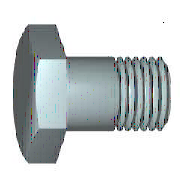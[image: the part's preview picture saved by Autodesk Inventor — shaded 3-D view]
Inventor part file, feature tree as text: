
AUTODESK INVENTOR PART (.ipt)
format: ipt  version: 2024.2 (Build 282272000, 272)  size: 202,752 bytes
history: native  units: mm (DEFAULTED — no unit token found)
features: other x4, plane x3, sketch x2, chamfer x1, fillet x1
ambient origin geometry x6: Origin, XY Plane, X Axis, Y Axis, Z Axis, Center Point
bodies: Solid1 (feature_tree)
feature tree (11):
  plane  "WorkPlane1"
  sketch  "Sketch1"  dims[d0=30.0mm]
  other  "WorkPoint1"
  chamfer  "Chamfer1"  Distance=15.0mm
  fillet  "Fillet1"  Radius=17.321016mm
  other  "MSC_A1"
  other  "MSC_PF1"
  other  "MSC_PT1"
  plane  "WorkPlane2"
  plane  "WorkPlane3"
  sketch  "Sketch2"  dims[d1=16.0mm d2=15.0mm d4=17.321016mm d6=6.4mm d7=0.0mm d8=15.0mm d10=0.0mm d12=30.0deg d14=360.0deg d15=0.0mm d17=10.0mm d18=5.0mm d19=80.0mm d20=20.0mm d21=360.0deg d22=0.75mm d23=0.75mm d24=0.4mm d25=0.1mm d26=0.0mm d27=60.0deg d28=8.0mm d29=0.0mm d30=0.0mm d32=0.0mm d33=0.0mm d34=0.0mm d37=0.0mm d38=0.0mm d39=45.0deg d40=0.0mm d41=0.0mm d42=0.0mm]
